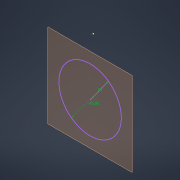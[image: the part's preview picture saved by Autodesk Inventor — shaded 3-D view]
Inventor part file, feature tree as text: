
AUTODESK INVENTOR PART (.ipt)
format: ipt  version: 2022 (Build 260153070, 153G)  size: 102,400 bytes
history: native  units: mm
features: extrude x1, sketch x1
ambient origin geometry x8: Origin, YZ Plane, XZ Plane, XY Plane, X Axis, Y Axis, Z Axis, Center Point
bodies: Body1 (feature_tree)
feature tree (2):
  extrude  "Выдавливание2"  Depth=5.0mm
  sketch  "Эскиз4"
